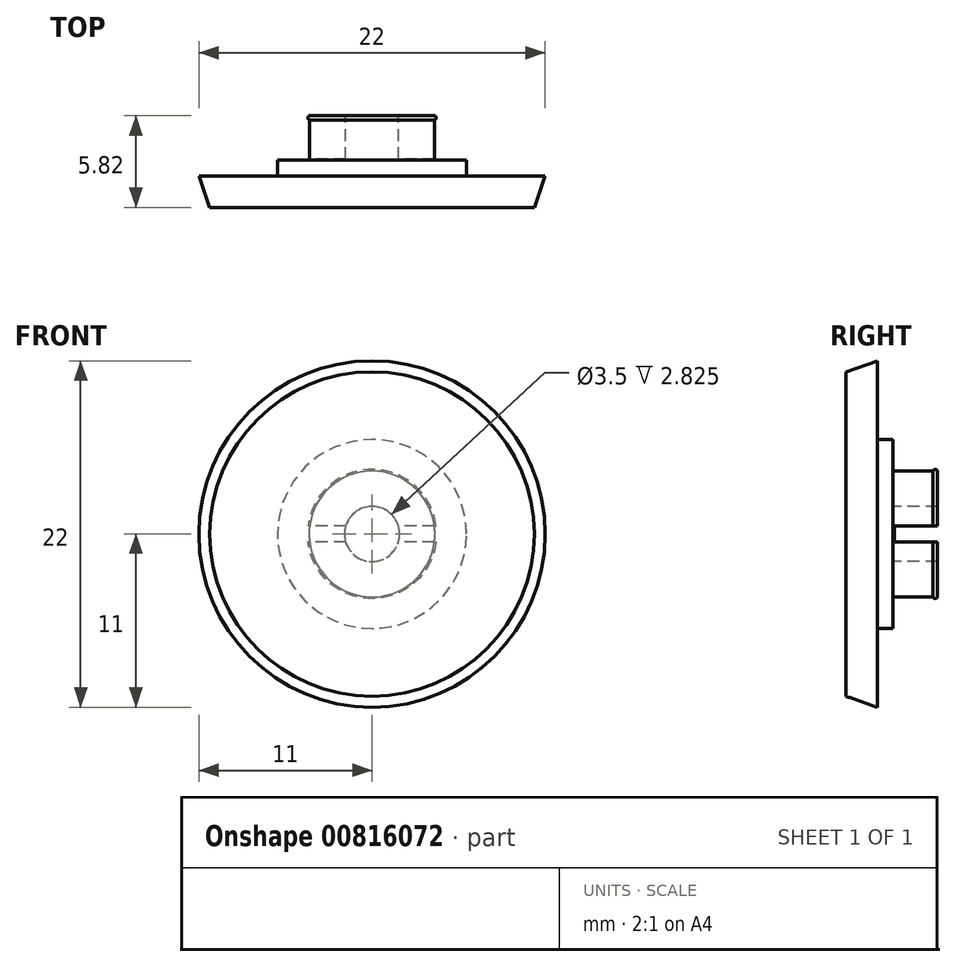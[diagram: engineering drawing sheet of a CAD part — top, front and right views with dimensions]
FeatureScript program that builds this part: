
annotation { "Feature Type Name" : "Feature", "Feature Type Description" : "" }
export const myFeature = defineFeature(function(context is Context, id is Id, definition is map)
    precondition{}
    {
        {
            var Q0;
            Q0=qCreatedBy(makeId("Top.planeOp"),FACE);
            var sketch = newSketch(context, id + "F0", { "sketchPlane" : qUnion([Q0])});
            skLineSegment(sketch, "E0.bottom", {"start": v(0, 0) * mm, "end": v(-10.3, 0) * mm});
            skLineSegment(sketch, "E0.top", {"start": v(-6, 2) * mm, "end": v(-11, 2) * mm});
            skLineSegment(sketch, "E0.left", {"start": v(0, 0) * mm, "end": v(0, 2) * mm});
            skLineSegment(sketch, "E1.top", {"start": v(0, 3) * mm, "end": v(-1.75, 3) * mm});
            skLineSegment(sketch, "E1.left", {"start": v(0, 2) * mm, "end": v(0, 3) * mm});
            skLineSegment(sketch, "E1.right", {"start": v(-6, 2) * mm, "end": v(-6, 3) * mm});
            skLineSegment(sketch, "E2.top", {"start": v(-4, 5.82) * mm, "end": v(-1.75, 5.82) * mm});
            skLineSegment(sketch, "E2.left", {"start": v(-4, 3) * mm, "end": v(-4, 5.54) * mm});
            skLineSegment(sketch, "E2.right", {"start": v(-1.75, 3) * mm, "end": v(-1.75, 5.82) * mm});
            skLineSegment(sketch, "E3.bottom", {"start": v(-1.75, 3) * mm, "end": v(0, 3) * mm});
            skLineSegment(sketch, "E3.top", {"start": v(-1.75, 3) * mm, "end": v(0, 3) * mm});
            skLineSegment(sketch, "E3.left", {"start": v(-1.75, 3) * mm, "end": v(-1.75, 3) * mm});
            skLineSegment(sketch, "E3.right", {"start": v(0, 3) * mm, "end": v(0, 3) * mm});
            skLineSegment(sketch, "E4", {"start": v(-11, 2) * mm, "end": v(-10.3, 0) * mm});
            skArc(sketch, "E5", {"start": v(-4, 5.82) * mm, "mid": v(-4.1, 5.68) * mm, "end": v(-4, 5.54) * mm});
            skPoint(sketch, "E5.second.point", {"position": v(-4, 5.54) * mm});
            skPoint(sketch, "E5.third.point", {"position": v(-4.09, 5.61) * mm});
            skLineSegment(sketch, "E6.trimOffspring", {"start": v(-4, 3) * mm, "end": v(-6, 3) * mm});
            skSolve(sketch);
        }
        {
            var Q0;
            Q0=makeQuery(id+"F0.imprint","IMPRINT",FACE,{"disambiguationData":[TD([[makeQuery(id+"F0.imprint","IMPRINT",EDGE,{"derivedFrom":sQuery(id+"F0.wireOp",EDGE,"E0.bottom")}),-1.0]])]});
            var Q1;
            Q1=sQuery(id+"F0.wireOp",EDGE,"E1.left");
            revolve(context, id + "F1", {"surfaceOperationType" : NewSurfaceOperationType.NEW, "entities" : qUnion([Q0]), "axis" : qUnion([Q1]), "revolveType" : RevolveType.FULL});
        }
        {
            var Q0;
            Q0=makeQuery(id+"F1.opRevolve","SWEPT_FACE",FACE,{"disambiguationData":[OSD([sQuery(id+"F0.wireOp",EDGE,"E2.top")])]});
            var sketch = newSketch(context, id + "F2", { "sketchPlane" : qUnion([Q0])});
            skLineSegment(sketch, "E7.bottom", {"start": v(-4.51, -0.5) * mm, "end": v(4.51, -0.5) * mm});
            skLineSegment(sketch, "E7.top", {"start": v(-4.51, 0.5) * mm, "end": v(4.51, 0.5) * mm});
            skLineSegment(sketch, "E7.left", {"start": v(-4.51, -0.5) * mm, "end": v(-4.51, 0.5) * mm});
            skLineSegment(sketch, "E7.right", {"start": v(4.51, -0.5) * mm, "end": v(4.51, 0.5) * mm});
            skPoint(sketch, "E7.middle", {"position": v(0, 0) * mm});
            skSolve(sketch);
        }
        {
            var Q0;
            {var subQ0=sQuery(id+"F2.wireOp",EDGE,"E7.left");Q0=makeQuery(id+"F2.imprint","IMPRINT",FACE,{"disambiguationData":[TD([[makeQuery(id+"F2.imprint","IMPRINT",EDGE,{"derivedFrom":subQ0}),-1.0]])]});}
            var Q1;
            {var subQ0=sQuery(id+"F2.wireOp",EDGE,"E7.bottom");var subQ1=sQuery(id+"F0.wireOp",EDGE,"E2.top");var subQ2=makeQuery(id+"F1.opRevolve","SWEPT_EDGE",EDGE,{"disambiguationData":[OSD([subQ1,sQuery(id+"F0.wireOp",EDGE,"E5")])]});var subQ3=makeQuery(id+"F2.imprint","INTERSECT",VERTEX,{"disambiguationData":[OD(0.0)],"derivedFrom":[subQ2,subQ0]});Q1=makeQuery(id+"F2.imprint","IMPRINT",FACE,{"disambiguationData":[TD([[makeQuery(id+"F2.imprint","IMPRINT",EDGE,{"disambiguationData":[TD([[subQ3,-1.0]])],"derivedFrom":subQ0}),1.0]])]});}
            var Q2;
            {var subQ0=sQuery(id+"F2.wireOp",EDGE,"E7.bottom");var subQ1=sQuery(id+"F0.wireOp",EDGE,"E2.top");var subQ2=makeQuery(id+"F1.opRevolve","SWEPT_EDGE",EDGE,{"disambiguationData":[OSD([subQ1,sQuery(id+"F0.wireOp",EDGE,"E5")])]});var subQ3=makeQuery(id+"F2.imprint","INTERSECT",VERTEX,{"disambiguationData":[OD(1.0)],"derivedFrom":[subQ2,subQ0]});Q2=makeQuery(id+"F2.imprint","IMPRINT",FACE,{"disambiguationData":[TD([[makeQuery(id+"F2.imprint","IMPRINT",EDGE,{"disambiguationData":[TD([[subQ3,1.0]])],"derivedFrom":subQ0}),1.0]])]});}
            var Q3;
            {var subQ0=sQuery(id+"F2.wireOp",EDGE,"E7.right");Q3=makeQuery(id+"F2.imprint","IMPRINT",FACE,{"disambiguationData":[TD([[makeQuery(id+"F2.imprint","IMPRINT",EDGE,{"derivedFrom":subQ0}),1.0]])]});}
            extrude(context, id + "F3", {"entities" : qUnion([Q0, Q1, Q2, Q3]), "operationType" : NewBodyOperationType.REMOVE, "oppositeDirection" : true, "depth" : 2.75 * mm, "offsetDistance" : 25 * mm});
        }
    });
